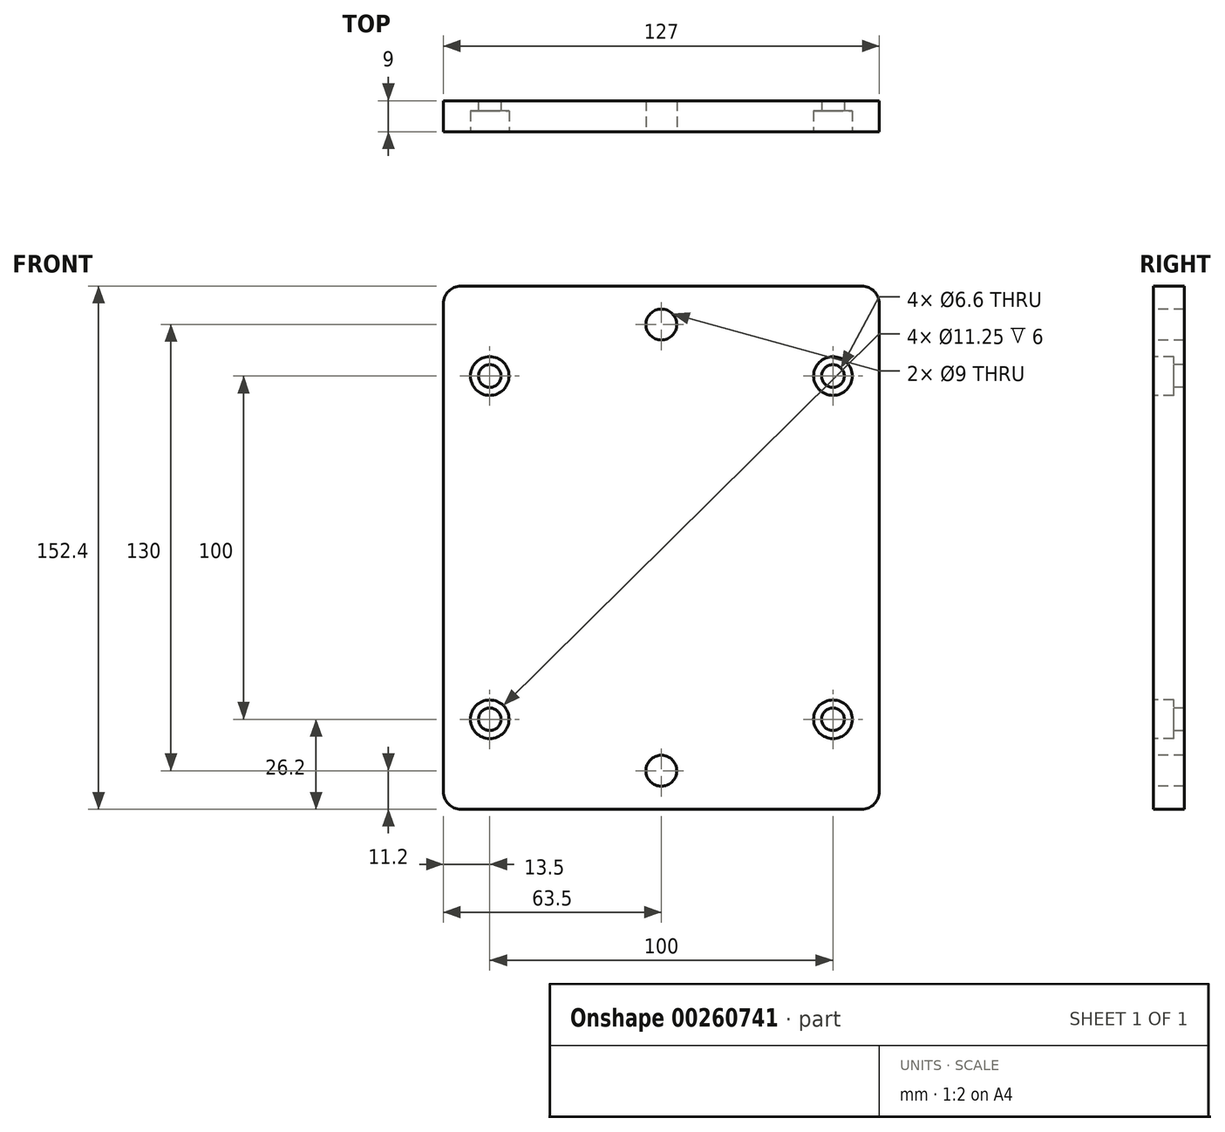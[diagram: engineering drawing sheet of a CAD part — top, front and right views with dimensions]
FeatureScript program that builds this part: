
annotation { "Feature Type Name" : "Feature", "Feature Type Description" : "" }
export const myFeature = defineFeature(function(context is Context, id is Id, definition is map)
    precondition{}
    {
        {
            var Q0;
            Q0=qCreatedBy(makeId("Front.planeOp"),FACE);
            var sketch = newSketch(context, id + "F0", { "sketchPlane" : qUnion([Q0])});
            skLineSegment(sketch, "E0.bottom", {"start": v(63.5, -76.2) * mm, "end": v(-63.5, -76.2) * mm});
            skLineSegment(sketch, "E0.top", {"start": v(63.5, 76.2) * mm, "end": v(-63.5, 76.2) * mm});
            skLineSegment(sketch, "E0.left", {"start": v(63.5, -76.2) * mm, "end": v(63.5, 76.2) * mm});
            skLineSegment(sketch, "E0.right", {"start": v(-63.5, -76.2) * mm, "end": v(-63.5, 76.2) * mm});
            skPoint(sketch, "E0.middle", {"position": v(0, 0) * mm});
            skSolve(sketch);
        }
        {
            var Q0;
            Q0=makeQuery(id+"F0.imprint","IMPRINT",FACE,{"disambiguationData":[TD([[makeQuery(id+"F0.imprint","IMPRINT",EDGE,{"derivedFrom":sQuery(id+"F0.wireOp",EDGE,"E0.bottom")}),-1.0]])]});
            extrude(context, id + "F1", {"entities" : qUnion([Q0]), "depth" : 9 * mm});
        }
        {
            var Q0;
            Q0=makeQuery(id+"F1.opExtrude","CAP_FACE",FACE,{"disambiguationData":[OSD([sQuery(id+"F0.wireOp",EDGE,"E0.bottom"),sQuery(id+"F0.wireOp",EDGE,"E0.top"),sQuery(id+"F0.wireOp",EDGE,"E0.left"),sQuery(id+"F0.wireOp",EDGE,"E0.right")])],"isStart":false});
            var sketch = newSketch(context, id + "F2", { "sketchPlane" : qUnion([Q0])});
            skPoint(sketch, "E1", {"position": v(0, 0) * mm});
            skPoint(sketch, "E2", {"position": v(0, 65) * mm});
            skPoint(sketch, "E3", {"position": v(0, -65) * mm});
            skSolve(sketch);
        }
        {
            var Q0;
            Q0=sQuery(id+"F2.wireOp",VERTEX,"E2");
            var Q1;
            Q1=sQuery(id+"F2.wireOp",VERTEX,"E3");
            var Q2;
            Q2=makeQuery(id+"F1.opExtrude","SWEPT_BODY",BODY,{"disambiguationData":[OSD([sQuery(id+"F0.wireOp",EDGE,"E0.bottom"),sQuery(id+"F0.wireOp",EDGE,"E0.top"),sQuery(id+"F0.wireOp",EDGE,"E0.left"),sQuery(id+"F0.wireOp",EDGE,"E0.right")])]});
            hole(context, id + "F3", {"style" : HoleStyle.SIMPLE, "endStyle" : HoleEndStyle.THROUGH, "standardTappedOrClearance" : lookupTablePath({ "standard" : "ISO", "engagement" : "75%", "pitch" : "1 mm", "size" : "M10", "type" : "Tapped" }), "standardBlindInLast" : lookupTablePath({ "standard" : "ISO", "engagement" : "75%", "pitch" : "1 mm", "size" : "M10", "type" : "Tapped" }), "holeDiameter" : 9 * mm, "showTappedDepth" : true, "tappedDepth" : 12.7 * mm, "tapClearance" : 3, "locations" : qUnion([Q0, Q1]), "scope" : qUnion([Q2]), "majorDiameter" : 10 * mm});
        }
        {
            var Q0;
            Q0=makeQuery(id+"F1.opExtrude","CAP_FACE",FACE,{"disambiguationData":[OSD([sQuery(id+"F0.wireOp",EDGE,"E0.bottom"),sQuery(id+"F0.wireOp",EDGE,"E0.top"),sQuery(id+"F0.wireOp",EDGE,"E0.left"),sQuery(id+"F0.wireOp",EDGE,"E0.right")])],"isStart":false});
            var sketch = newSketch(context, id + "F4", { "sketchPlane" : qUnion([Q0])});
            skPoint(sketch, "E4", {"position": v(-50, -50) * mm});
            skPoint(sketch, "E5", {"position": v(50, -50) * mm});
            skPoint(sketch, "E6", {"position": v(-50, 50) * mm});
            skPoint(sketch, "E7", {"position": v(50, 50) * mm});
            skSolve(sketch);
        }
        {
            var Q0;
            Q0=sQuery(id+"F4.wireOp",VERTEX,"E6");
            var Q1;
            Q1=sQuery(id+"F4.wireOp",VERTEX,"E7");
            var Q2;
            Q2=sQuery(id+"F4.wireOp",VERTEX,"E5");
            var Q3;
            Q3=sQuery(id+"F4.wireOp",VERTEX,"E4");
            var Q4;
            Q4=makeQuery(id+"F1.opExtrude","SWEPT_BODY",BODY,{"disambiguationData":[OSD([sQuery(id+"F0.wireOp",EDGE,"E0.bottom"),sQuery(id+"F0.wireOp",EDGE,"E0.top"),sQuery(id+"F0.wireOp",EDGE,"E0.left"),sQuery(id+"F0.wireOp",EDGE,"E0.right")])]});
            hole(context, id + "F5", {"style" : HoleStyle.C_BORE, "endStyle" : HoleEndStyle.THROUGH, "standardTappedOrClearance" : lookupTablePath({ "standard" : "ISO", "fit" : "Normal", "size" : "M6", "type" : "Clearance" }), "standardBlindInLast" : lookupTablePath({ "fit" : "Standard", "standard" : "ISO", "size" : "M6", "type" : "Clearance" }), "holeDiameter" : 6.6 * mm, "cBoreDiameter" : 11.25 * mm, "cBoreDepth" : 6 * mm, "tappedDepth" : 12.7 * mm, "tapClearance" : 3, "locations" : qUnion([Q0, Q1, Q2, Q3]), "scope" : qUnion([Q4])});
        }
        {
            var Q0;
            Q0=makeQuery(id+"F1.opExtrude","SWEPT_EDGE",EDGE,{"disambiguationData":[OSD([sQuery(id+"F0.wireOp",EDGE,"E0.top"),sQuery(id+"F0.wireOp",EDGE,"E0.left")])]});
            var Q1;
            Q1=makeQuery(id+"F1.opExtrude","SWEPT_EDGE",EDGE,{"disambiguationData":[OSD([sQuery(id+"F0.wireOp",EDGE,"E0.bottom"),sQuery(id+"F0.wireOp",EDGE,"E0.left")])]});
            var Q2;
            Q2=makeQuery(id+"F1.opExtrude","SWEPT_EDGE",EDGE,{"disambiguationData":[OSD([sQuery(id+"F0.wireOp",EDGE,"E0.bottom"),sQuery(id+"F0.wireOp",EDGE,"E0.right")])]});
            var Q3;
            Q3=makeQuery(id+"F1.opExtrude","SWEPT_EDGE",EDGE,{"disambiguationData":[OSD([sQuery(id+"F0.wireOp",EDGE,"E0.top"),sQuery(id+"F0.wireOp",EDGE,"E0.right")])]});
            fillet(context, id + "F6", {"entities" : qUnion([Q0, Q1, Q2, Q3]), "radius" : 5.08 * mm, "tangentPropagation" : true, "allowEdgeOverflow" : false});
        }
    });
